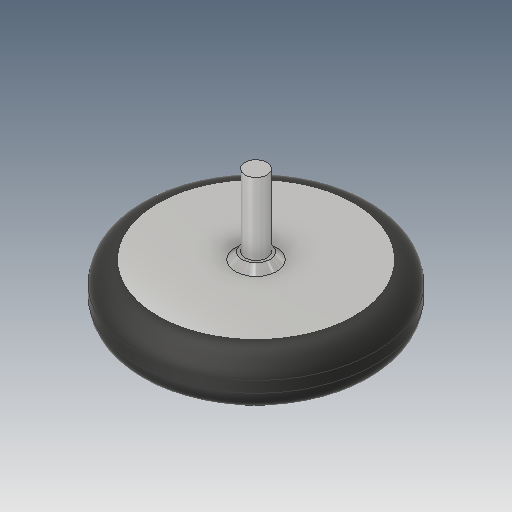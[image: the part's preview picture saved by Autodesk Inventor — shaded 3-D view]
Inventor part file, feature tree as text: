
AUTODESK INVENTOR PART (.ipt)
format: ipt  version: 2018 (Build 220112000, 112)  size: 164,864 bytes
history: native  units: in
note: dims shown in document units (in); Inventor stores cm internally (conversion verified against a paired STEP export)
features: other x3, sketch x3
ambient origin geometry x8: Origin, YZ Plane, XZ Plane, XY Plane, X Axis, Y Axis, Z Axis, Center Point
bodies: Solid1 (feature_tree)
feature tree (6):
  other  "10-001-ACTR.ipt"
  other  "Solid1::10-001-ACTR.ipt"
  other  "TaggingFeature1"
  sketch  "Sketch1"  dims[d0=0.3937in]
  sketch  "Sketch2"
  sketch  "Sketch3"
